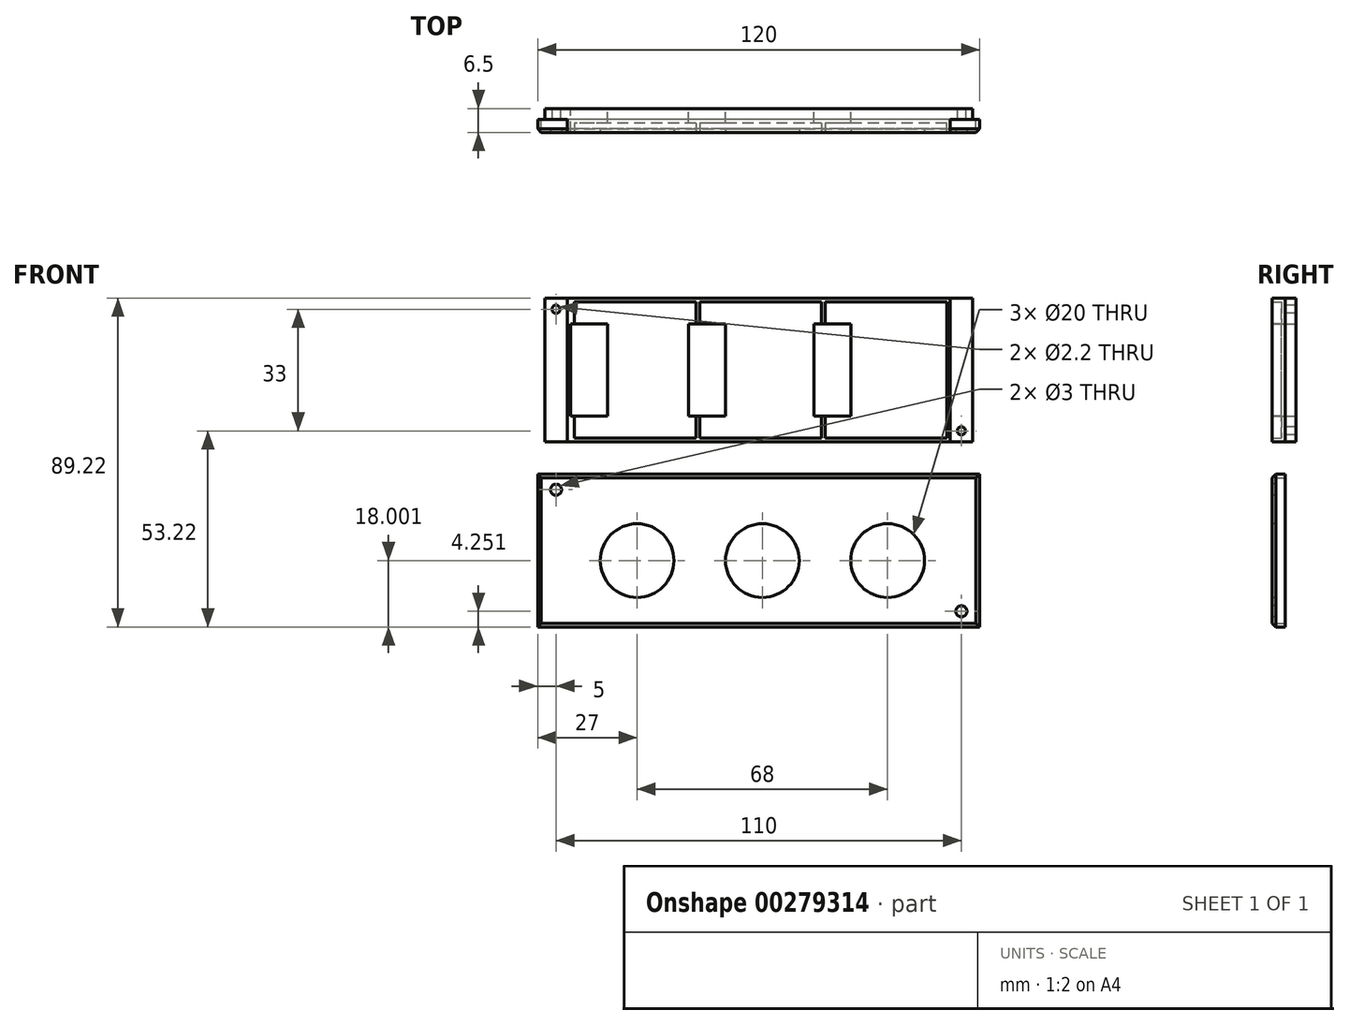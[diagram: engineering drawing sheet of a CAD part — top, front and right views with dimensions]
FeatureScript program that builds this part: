
annotation { "Feature Type Name" : "Feature", "Feature Type Description" : "" }
export const myFeature = defineFeature(function(context is Context, id is Id, definition is map)
    precondition{}
    {
        {
            var Q0;
            Q0=qCreatedBy(makeId("Front.planeOp"),FACE);
            var sketch = newSketch(context, id + "F0", { "sketchPlane" : qUnion([Q0])});
            skLineSegment(sketch, "E0.bottom", {"start": v(52, -19.5) * mm, "end": v(-52, -19.5) * mm});
            skLineSegment(sketch, "E0.top", {"start": v(52, 19.5) * mm, "end": v(-52, 19.5) * mm});
            skLineSegment(sketch, "E0.left", {"start": v(52, -19.5) * mm, "end": v(52, 19.5) * mm});
            skLineSegment(sketch, "E0.right", {"start": v(-52, -19.5) * mm, "end": v(-52, 19.5) * mm});
            skPoint(sketch, "E0.middle", {"position": v(0, 0) * mm});
            skSolve(sketch);
        }
        {
            var Q0;
            Q0 = qSketchRegion(id + "F0", true);
            extrude(context, id + "F1", {"entities" : qUnion([Q0]), "depth" : 3.5 * mm});
        }
        {
            var Q0;
            Q0=makeQuery(id+"F1.opExtrude","CAP_FACE",FACE,{"disambiguationData":[OSD([sQuery(id+"F0.wireOp",EDGE,"E0.bottom"),sQuery(id+"F0.wireOp",EDGE,"E0.top"),sQuery(id+"F0.wireOp",EDGE,"E0.left"),sQuery(id+"F0.wireOp",EDGE,"E0.right")])],"isStart":false});
            shell(context, id + "F2", {"entities" : qUnion([Q0]), "thickness" : 1 * mm});
        }
        {
            var Q0;
            Q0=makeQuery(id+"F2.opShell","OFFSET_FACE",FACE,{"disambiguationData":[OSD([sQuery(id+"F0.wireOp",EDGE,"E0.bottom"),sQuery(id+"F0.wireOp",EDGE,"E0.top"),sQuery(id+"F0.wireOp",EDGE,"E0.left"),sQuery(id+"F0.wireOp",EDGE,"E0.right")])]});
            var sketch = newSketch(context, id + "F3", { "sketchPlane" : qUnion([Q0])});
            skLineSegment(sketch, "E1.bottom", {"start": v(-17, 18.5) * mm, "end": v(-16, 18.5) * mm});
            skLineSegment(sketch, "E1.top", {"start": v(-17, -18.5) * mm, "end": v(-16, -18.5) * mm});
            skLineSegment(sketch, "E1.left", {"start": v(-17, 18.5) * mm, "end": v(-17, -18.5) * mm});
            skLineSegment(sketch, "E1.right", {"start": v(-16, 18.5) * mm, "end": v(-16, -18.5) * mm});
            skLineSegment(sketch, "E2.bottom", {"start": v(17, 18.5) * mm, "end": v(18, 18.5) * mm});
            skLineSegment(sketch, "E2.top", {"start": v(17, -18.5) * mm, "end": v(18, -18.5) * mm});
            skLineSegment(sketch, "E2.left", {"start": v(17, 18.5) * mm, "end": v(17, -18.5) * mm});
            skLineSegment(sketch, "E2.right", {"start": v(18, 18.5) * mm, "end": v(18, -18.5) * mm});
            skLineSegment(sketch, "E3.bottom", {"start": v(-51, 18.5) * mm, "end": v(-50, 18.5) * mm});
            skLineSegment(sketch, "E3.top", {"start": v(-51, -18.5) * mm, "end": v(-50, -18.5) * mm});
            skLineSegment(sketch, "E3.left", {"start": v(-51, 18.5) * mm, "end": v(-51, -18.5) * mm});
            skLineSegment(sketch, "E3.right", {"start": v(-50, 18.5) * mm, "end": v(-50, -18.5) * mm});
            skSolve(sketch);
        }
        {
            var Q0;
            Q0 = qSketchRegion(id + "F3", true);
            extrude(context, id + "F4", {"entities" : qUnion([Q0]), "operationType" : NewBodyOperationType.ADD, "depth" : 2.5 * mm});
        }
        {
            var Q0;
            Q0=makeQuery(id+"F1.opExtrude","CAP_FACE",FACE,{"disambiguationData":[OSD([sQuery(id+"F0.wireOp",EDGE,"E0.bottom"),sQuery(id+"F0.wireOp",EDGE,"E0.top"),sQuery(id+"F0.wireOp",EDGE,"E0.left"),sQuery(id+"F0.wireOp",EDGE,"E0.right")])],"isStart":true});
            var sketch = newSketch(context, id + "F5", { "sketchPlane" : qUnion([Q0])});
            skLineSegment(sketch, "E4.bottom", {"start": v(-58, 19.5) * mm, "end": v(58, 19.5) * mm});
            skLineSegment(sketch, "E4.top", {"start": v(-58, -19.5) * mm, "end": v(58, -19.5) * mm});
            skLineSegment(sketch, "E4.left", {"start": v(-58, 19.5) * mm, "end": v(-58, -19.5) * mm});
            skLineSegment(sketch, "E4.right", {"start": v(58, 19.5) * mm, "end": v(58, -19.5) * mm});
            skCircle(sketch, "E5", {"center": v(55, 16.5) * mm, "radius": 1.1 * mm});
            skCircle(sketch, "E6", {"center": v(55, -16.5) * mm, "radius": 1.1 * mm, "construction": true});
            skCircle(sketch, "E7", {"center": v(-55, 16.5) * mm, "radius": 1.1 * mm, "construction": true});
            skCircle(sketch, "E8", {"center": v(-55, -16.5) * mm, "radius": 1.1 * mm});
            skSolve(sketch);
        }
        {
            var Q0;
            Q0 = qSketchRegion(id + "F5", true);
            extrude(context, id + "F6", {"entities" : qUnion([Q0]), "operationType" : NewBodyOperationType.ADD, "depth" : 3 * mm});
        }
        {
            var Q0;
            Q0=qCreatedBy(makeId("Front.planeOp"),FACE);
            var sketch = newSketch(context, id + "F7", { "sketchPlane" : qUnion([Q0])});
            skLineSegment(sketch, "E9.bottom", {"start": v(-51, 12.5) * mm, "end": v(-41, 12.5) * mm});
            skLineSegment(sketch, "E9.top", {"start": v(-51, -12.5) * mm, "end": v(-41, -12.5) * mm});
            skLineSegment(sketch, "E9.left", {"start": v(-51, 12.5) * mm, "end": v(-51, -12.5) * mm});
            skLineSegment(sketch, "E9.right", {"start": v(-41, 12.5) * mm, "end": v(-41, -12.5) * mm});
            skLineSegment(sketch, "E10.bottom", {"start": v(-19, 12.5) * mm, "end": v(-9, 12.5) * mm});
            skLineSegment(sketch, "E10.top", {"start": v(-19, -12.5) * mm, "end": v(-9, -12.5) * mm});
            skLineSegment(sketch, "E10.left", {"start": v(-19, 12.5) * mm, "end": v(-19, -12.5) * mm});
            skLineSegment(sketch, "E10.right", {"start": v(-9, 12.5) * mm, "end": v(-9, -12.5) * mm});
            skLineSegment(sketch, "E11.bottom", {"start": v(15, 12.5) * mm, "end": v(25, 12.5) * mm});
            skLineSegment(sketch, "E11.top", {"start": v(15, -12.5) * mm, "end": v(25, -12.5) * mm});
            skLineSegment(sketch, "E11.left", {"start": v(15, 12.5) * mm, "end": v(15, -12.5) * mm});
            skLineSegment(sketch, "E11.right", {"start": v(25, 12.5) * mm, "end": v(25, -12.5) * mm});
            skSolve(sketch);
        }
        {
            var Q0;
            Q0 = qSketchRegion(id + "F7", true);
            extrude(context, id + "F8", {"entities" : qUnion([Q0]), "operationType" : NewBodyOperationType.REMOVE, "endBound" : BoundingType.SYMMETRIC, "depth" : 11.2 * mm});
        }
        {
            var Q0;
            Q0=qCreatedBy(makeId("Front.planeOp"),FACE);
            var sketch = newSketch(context, id + "F9", { "sketchPlane" : qUnion([Q0])});
            skLineSegment(sketch, "E12.bottom", {"start": v(60, -69.72) * mm, "end": v(-60, -69.72) * mm});
            skLineSegment(sketch, "E12.top", {"start": v(60, -28.22) * mm, "end": v(-60, -28.22) * mm});
            skLineSegment(sketch, "E12.left", {"start": v(60, -69.72) * mm, "end": v(60, -28.22) * mm});
            skLineSegment(sketch, "E12.right", {"start": v(-60, -69.72) * mm, "end": v(-60, -28.22) * mm});
            skPoint(sketch, "E12.middle", {"position": v(0, -48.97) * mm});
            skSolve(sketch);
        }
        {
            var Q0;
            Q0 = qSketchRegion(id + "F9", true);
            extrude(context, id + "F10", {"entities" : qUnion([Q0]), "depth" : 3.5 * mm});
        }
        {
            var Q0;
            Q0=makeQuery(id+"F10.opExtrude","CAP_FACE",FACE,{"disambiguationData":[OSD([sQuery(id+"F9.wireOp",EDGE,"E12.bottom"),sQuery(id+"F9.wireOp",EDGE,"E12.top"),sQuery(id+"F9.wireOp",EDGE,"E12.left"),sQuery(id+"F9.wireOp",EDGE,"E12.right")])],"isStart":true});
            shell(context, id + "F11", {"entities" : qUnion([Q0]), "thickness" : 1 * mm});
        }
        {
            var Q0;
            Q0=makeQuery(id+"F10.opExtrude","CAP_FACE",FACE,{"disambiguationData":[OSD([sQuery(id+"F9.wireOp",EDGE,"E12.bottom"),sQuery(id+"F9.wireOp",EDGE,"E12.top"),sQuery(id+"F9.wireOp",EDGE,"E12.left"),sQuery(id+"F9.wireOp",EDGE,"E12.right")])],"isStart":false});
            var sketch = newSketch(context, id + "F12", { "sketchPlane" : qUnion([Q0])});
            skCircle(sketch, "E13", {"center": v(55, -65.47) * mm, "radius": 1.5 * mm});
            skCircle(sketch, "E14", {"center": v(-55, -32.47) * mm, "radius": 1.5 * mm});
            skCircle(sketch, "E15", {"center": v(-33, -51.72) * mm, "radius": 10 * mm});
            skCircle(sketch, "E16", {"center": v(1, -51.72) * mm, "radius": 10 * mm});
            skCircle(sketch, "E17", {"center": v(35, -51.72) * mm, "radius": 10 * mm});
            skSolve(sketch);
        }
        {
            var Q0;
            Q0 = qSketchRegion(id + "F12", true);
            extrude(context, id + "F13", {"entities" : qUnion([Q0]), "operationType" : NewBodyOperationType.REMOVE, "oppositeDirection" : true, "depth" : 1 * mm});
        }
        {
            var Q0;
            Q0=makeQuery(id+"F10.opExtrude","CAP_EDGE",EDGE,{"disambiguationData":[OSD([sQuery(id+"F9.wireOp",EDGE,"E12.top")])],"isStart":false});
            var Q1;
            Q1=makeQuery(id+"F10.opExtrude","CAP_EDGE",EDGE,{"disambiguationData":[OSD([sQuery(id+"F9.wireOp",EDGE,"E12.right")])],"isStart":false});
            var Q2;
            Q2=makeQuery(id+"F10.opExtrude","CAP_EDGE",EDGE,{"disambiguationData":[OSD([sQuery(id+"F9.wireOp",EDGE,"E12.left")])],"isStart":false});
            var Q3;
            Q3=makeQuery(id+"F10.opExtrude","CAP_EDGE",EDGE,{"disambiguationData":[OSD([sQuery(id+"F9.wireOp",EDGE,"E12.bottom")])],"isStart":false});
            chamfer(context, id + "F14", {"entities" : qUnion([Q0, Q1, Q2, Q3]), "width" : 1 * mm, "tangentPropagation" : true});
        }
    });
